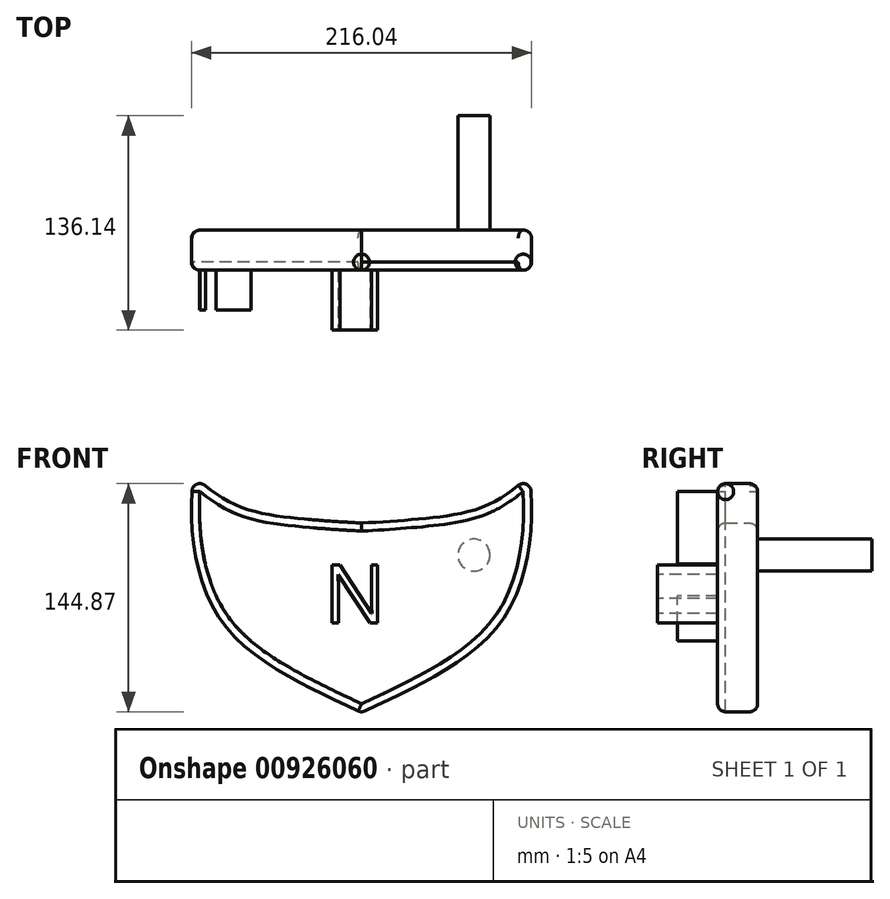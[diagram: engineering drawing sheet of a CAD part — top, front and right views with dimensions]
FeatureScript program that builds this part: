
annotation { "Feature Type Name" : "Feature", "Feature Type Description" : "" }
export const myFeature = defineFeature(function(context is Context, id is Id, definition is map)
    precondition{}
    {
        {
            var Q0;
            Q0=qCreatedBy(makeId("Front.planeOp"),FACE);
            var sketch = newSketch(context, id + "F0", { "sketchPlane" : qUnion([Q0])});
            skLineSegment(sketch, "E0", {"start": v(0, 53.5) * mm, "end": v(0, -66.83) * mm});
            skFitSpline(sketch, "E1", {"points": [v(-107.19, 83.77) * mm, v(-80.88, 65.4) * mm, v(-46.3, 57.1) * mm, v(0, 53.5) * mm], "startDerivative": vector(81.22, -67.73) * mm, "endDerivative": vector(128.95, -7.74) * mm});
            skFitSpline(sketch, "E2", {"points": [v(-107.19, 83.77) * mm, v(-107.19, 44.86) * mm, v(-85.57, -13.15) * mm, v(0, -66.83) * mm], "startDerivative": vector(-8.43, -141.7) * mm, "endDerivative": vector(241.74, -112.08) * mm});
            skFitSpline(sketch, "E3.MirrorCS", {"points": [v(107.19, 83.77) * mm, v(80.88, 65.4) * mm, v(46.3, 57.1) * mm, v(0, 53.5) * mm], "startDerivative": vector(-81.22, -67.73) * mm, "endDerivative": vector(-128.95, -7.74) * mm});
            skFitSpline(sketch, "E4.MirrorCS", {"points": [v(107.19, 83.77) * mm, v(107.19, 44.86) * mm, v(85.57, -13.15) * mm, v(0, -66.83) * mm], "startDerivative": vector(8.43, -141.7) * mm, "endDerivative": vector(-241.74, -112.08) * mm});
            skSolve(sketch);
        }
        {
            var Q0;
            Q0=makeQuery(id+"F0.imprint","IMPRINT",FACE,{"disambiguationData":[TD([[makeQuery(id+"F0.imprint","IMPRINT",EDGE,{"derivedFrom":sQuery(id+"F0.wireOp",EDGE,"E0")}),-1.0]])]});
            var Q1;
            Q1=makeQuery(id+"F0.imprint","IMPRINT",FACE,{"disambiguationData":[TD([[makeQuery(id+"F0.imprint","IMPRINT",EDGE,{"derivedFrom":sQuery(id+"F0.wireOp",EDGE,"E0")}),1.0]])]});
            extrude(context, id + "F1", {"entities" : qUnion([Q0, Q1]), "depth" : 25.4 * mm, "offsetDistance" : 25.4 * mm});
        }
        {
            var Q0;
            Q0=makeQuery(id+"F1.opExtrude","CAP_EDGE",EDGE,{"disambiguationData":[OSD([sQuery(id+"F0.wireOp",EDGE,"E2")])],"isStart":true});
            var Q1;
            Q1=makeQuery(id+"F1.opExtrude","CAP_EDGE",EDGE,{"disambiguationData":[OSD([sQuery(id+"F0.wireOp",EDGE,"E2")])],"isStart":false});
            fillet(context, id + "F2", {"entities" : qUnion([Q0, Q1]), "radius" : 5.08 * mm, "tangentPropagation" : true, "allowEdgeOverflow" : false});
        }
        {
            var Q0;
            Q0=makeQuery(id+"F1.opExtrude","CAP_EDGE",EDGE,{"disambiguationData":[OSD([sQuery(id+"F0.wireOp",EDGE,"E3.MirrorCS")])],"isStart":true});
            var Q1;
            Q1=makeQuery(id+"F1.opExtrude","CAP_FACE",FACE,{"disambiguationData":[OSD([sQuery(id+"F0.wireOp",EDGE,"E1"),sQuery(id+"F0.wireOp",EDGE,"E2"),sQuery(id+"F0.wireOp",EDGE,"E3.MirrorCS"),sQuery(id+"F0.wireOp",EDGE,"E4.MirrorCS")])],"isStart":false});
            fillet(context, id + "F3", {"entities" : qUnion([Q0, Q1]), "radius" : 5.08 * mm, "tangentPropagation" : true, "allowEdgeOverflow" : false});
        }
        {
            var Q0;
            Q0=makeQuery(id+"F3.opFillet","BLEND_EDGE",EDGE,{"blendedFrom":[makeQuery(id+"F1.opExtrude","CAP_EDGE",EDGE,{"disambiguationData":[OSD([sQuery(id+"F0.wireOp",EDGE,"E3.MirrorCS")])],"isStart":false}),makeQuery(id+"F1.opExtrude","CAP_EDGE",EDGE,{"disambiguationData":[OSD([sQuery(id+"F0.wireOp",EDGE,"E4.MirrorCS")])],"isStart":false})],"blendedInto":[]});
            var Q1;
            {var subQ0=sQuery(id+"F0.wireOp",EDGE,"E1");Q1=makeQuery(id+"F3.opFillet","BLEND_EDGE",EDGE,{"blendedFrom":[makeQuery(id+"F1.opExtrude","CAP_EDGE",EDGE,{"disambiguationData":[OSD([subQ0])],"isStart":false}),makeQuery(id+"F1.opExtrude","SWEPT_FACE",FACE,{"disambiguationData":[OSD([subQ0])]})],"blendedInto":[makeQuery(id+"F1.opExtrude","SWEPT_FACE",FACE,{"disambiguationData":[OSD([subQ0])]})]});}
            var Q2;
            {var subQ0=sQuery(id+"F0.wireOp",EDGE,"E2");Q2=makeQuery(id+"F2.opFillet","BLEND_EDGE",EDGE,{"blendedFrom":[makeQuery(id+"F1.opExtrude","CAP_EDGE",EDGE,{"disambiguationData":[OSD([subQ0])],"isStart":true}),makeQuery(id+"F1.opExtrude","SWEPT_FACE",FACE,{"disambiguationData":[OSD([subQ0])]})],"blendedInto":[makeQuery(id+"F1.opExtrude","SWEPT_FACE",FACE,{"disambiguationData":[OSD([subQ0])]})]});}
            var Q3;
            {var subQ0=sQuery(id+"F0.wireOp",EDGE,"E1");var subQ1=sQuery(id+"F0.wireOp",EDGE,"E2");Q3=makeQuery(id+"F3.opFillet","BLEND_EDGE",EDGE,{"blendedFrom":[makeQuery(id+"F1.opExtrude","SWEPT_EDGE",EDGE,{"disambiguationData":[OSD([subQ0,subQ1])]}),makeQuery(id+"F2.opFillet","BLEND_EDGE",EDGE,{"blendedFrom":[makeQuery(id+"F1.opExtrude","CAP_EDGE",EDGE,{"disambiguationData":[OSD([subQ1])],"isStart":false}),makeQuery(id+"F1.opExtrude","SWEPT_FACE",FACE,{"disambiguationData":[OSD([subQ0])]})],"blendedInto":[makeQuery(id+"F1.opExtrude","SWEPT_FACE",FACE,{"disambiguationData":[OSD([subQ0])]})]})],"blendedInto":[]});}
            fillet(context, id + "F4", {"entities" : qUnion([Q0, Q1, Q2, Q3]), "radius" : 5.08 * mm, "tangentPropagation" : true, "allowEdgeOverflow" : false});
        }
        {
            var Q0;
            Q0=makeQuery(id+"F1.opExtrude","CAP_FACE",FACE,{"disambiguationData":[OSD([sQuery(id+"F0.wireOp",EDGE,"E1"),sQuery(id+"F0.wireOp",EDGE,"E2"),sQuery(id+"F0.wireOp",EDGE,"E3.MirrorCS"),sQuery(id+"F0.wireOp",EDGE,"E4.MirrorCS")])],"isStart":true});
            var sketch = newSketch(context, id + "F5", { "sketchPlane" : qUnion([Q0])});
            skSolve(sketch);
        }
        {
            var Q0;
            Q0=qCreatedBy(makeId("Front.planeOp"),FACE);
            var sketch = newSketch(context, id + "F6", { "sketchPlane" : qUnion([Q0])});
            skText(sketch, "E5", { "text": "DEVIL\n", "fontName": "OpenSans-Bold.ttf"});
            const initialGuessF6  = {"E5": [-0.04514, -0.01103, 1, 0, 0.03178]};
            skSetInitialGuess(sketch, initialGuessF6);
            skSolve(sketch);
        }
        {
            var Q0;
            Q0=qCreatedBy(makeId("Front.planeOp"),FACE);
            var sketch = newSketch(context, id + "F7", { "sketchPlane" : qUnion([Q0])});
            skSolve(sketch);
        }
        {
            var Q0;
            Q0 = qSketchRegion(id + "F6", true);
            var Q1;
            Q1=makeQuery(id+"F1.opExtrude","CAP_FACE",FACE,{"disambiguationData":[OSD([sQuery(id+"F0.wireOp",EDGE,"E1"),sQuery(id+"F0.wireOp",EDGE,"E2"),sQuery(id+"F0.wireOp",EDGE,"E3.MirrorCS"),sQuery(id+"F0.wireOp",EDGE,"E4.MirrorCS")])],"isStart":false});
            var Q2;
            {var subQ0=sQuery(id+"F0.wireOp",EDGE,"E4.MirrorCS");var subQ1=sQuery(id+"F0.wireOp",EDGE,"E3.MirrorCS");var subQ2=sQuery(id+"F0.wireOp",EDGE,"E2");var subQ3=sQuery(id+"F0.wireOp",EDGE,"E1");var subQ4=makeQuery(id+"F1.opExtrude","CAP_FACE",FACE,{"disambiguationData":[OSD([subQ3,subQ2,subQ1,subQ0])],"isStart":true});var subQ5=subQ4;Q2=makeQuery(id+"F5.imprint","IMPRINT",FACE,{"disambiguationData":[TD([[makeQuery(id+"F5.imprint","IMPRINT",EDGE,{"derivedFrom":makeQuery(id+"F3.opFillet","BLEND_EDGE",EDGE,{"blendedFrom":[makeQuery(id+"F1.opExtrude","CAP_EDGE",EDGE,{"disambiguationData":[OSD([subQ1])],"isStart":true}),subQ5],"blendedInto":[subQ5]})}),1.0]])]});}
            var Q3;
            Q3=makeQuery(id+"F6.imprint","IMPRINT",FACE,{"disambiguationData":[TD([[makeQuery(id+"F6.imprint","IMPRINT",EDGE,{"derivedFrom":sQuery(id+"F6.wireOp",EDGE,"E5.sketch_text.stroke-24")}),-1.0]])]});
            var Q4;
            Q4=makeQuery(id+"F6.imprint","IMPRINT",FACE,{"disambiguationData":[TD([[makeQuery(id+"F6.imprint","IMPRINT",EDGE,{"derivedFrom":sQuery(id+"F6.wireOp",EDGE,"E5.sketch_text.stroke-34")}),-1.0]])]});
            var Q5;
            Q5=makeQuery(id+"F1.opExtrude","CAP_FACE",FACE,{"disambiguationData":[OSD([sQuery(id+"F0.wireOp",EDGE,"E1"),sQuery(id+"F0.wireOp",EDGE,"E2"),sQuery(id+"F0.wireOp",EDGE,"E3.MirrorCS"),sQuery(id+"F0.wireOp",EDGE,"E4.MirrorCS")])],"isStart":true});
            var Q6;
            Q6=makeQuery(id+"F6.imprint","IMPRINT",FACE,{"disambiguationData":[TD([[makeQuery(id+"F6.imprint","IMPRINT",EDGE,{"derivedFrom":sQuery(id+"F6.wireOp",EDGE,"E5.sketch_text.stroke-0")}),-1.0]])]});
            var Q7;
            Q7=makeQuery(id+"F6.imprint","IMPRINT",FACE,{"disambiguationData":[TD([[makeQuery(id+"F6.imprint","IMPRINT",EDGE,{"derivedFrom":sQuery(id+"F6.wireOp",EDGE,"E5.sketch_text.stroke-7")}),1.0]])]});
            var Q8;
            Q8=makeQuery(id+"F6.imprint","IMPRINT",FACE,{"disambiguationData":[TD([[makeQuery(id+"F6.imprint","IMPRINT",EDGE,{"derivedFrom":sQuery(id+"F6.wireOp",EDGE,"E5.sketch_text.stroke-12")}),-1.0]])]});
            var Q9;
            Q9=makeQuery(id+"F6.imprint","IMPRINT",FACE,{"disambiguationData":[TD([[makeQuery(id+"F6.imprint","IMPRINT",EDGE,{"derivedFrom":sQuery(id+"F6.wireOp",EDGE,"E5.sketch_text.stroke-38")}),-1.0]])]});
            extrude(context, id + "F8", {"entities" : qUnion([Q0, Q1, Q2, Q3, Q4, Q5, Q6, Q7, Q8, Q9]), "operationType" : NewBodyOperationType.ADD, "depth" : 25.4 * mm, "offsetDistance" : 25.4 * mm});
        }
        {
            var Q0;
            {var subQ0=sQuery(id+"F0.wireOp",EDGE,"E4.MirrorCS");var subQ1=sQuery(id+"F0.wireOp",EDGE,"E3.MirrorCS");var subQ2=sQuery(id+"F0.wireOp",EDGE,"E2");var subQ3=sQuery(id+"F0.wireOp",EDGE,"E1");Q0=makeQuery(id+"F8.opExtrude","CAP_FACE",FACE,{"disambiguationData":[OSD([subQ3,subQ2,subQ1,subQ0]),TDD([makeQuery(id+"F1.opExtrude","CAP_FACE",FACE,{"disambiguationData":[OSD([subQ3,subQ2,subQ1,subQ0])],"isStart":false})])],"isStart":false});}
            var sketch = newSketch(context, id + "F9", { "sketchPlane" : qUnion([Q0])});
            skText(sketch, "E6", { "text": "N\n", "fontName": "OpenSans-Regular.ttf"});
            const initialGuessF9  = {"E6": [-0.02372, -0.01007, 1, 0, 0.0373]};
            skSetInitialGuess(sketch, initialGuessF9);
            skSolve(sketch);
        }
        {
            var Q0;
            Q0 = qSketchRegion(id + "F9", true);
            extrude(context, id + "F10", {"entities" : qUnion([Q0]), "operationType" : NewBodyOperationType.ADD, "depth" : 12.7 * mm, "offsetDistance" : 25.4 * mm});
        }
        {
            var Q0;
            Q0=qCreatedBy(makeId("Front.planeOp"),FACE);
            var sketch = newSketch(context, id + "F11", { "sketchPlane" : qUnion([Q0])});
            skCircle(sketch, "E7", {"center": v(80.37, 37.2) * mm, "radius": 12.45 * mm});
            skSolve(sketch);
        }
        {
            var Q0;
            Q0=makeQuery(id+"F11.imprint","IMPRINT",FACE,{"disambiguationData":[TD([[makeQuery(id+"F11.imprint","IMPRINT",EDGE,{"derivedFrom":sQuery(id+"F11.wireOp",EDGE,"E7")}),1.0]])]});
            var Q1;
            Q1=makeQuery(id+"F1.opExtrude","CAP_FACE",FACE,{"disambiguationData":[OSD([sQuery(id+"F0.wireOp",EDGE,"E1"),sQuery(id+"F0.wireOp",EDGE,"E2"),sQuery(id+"F0.wireOp",EDGE,"E3.MirrorCS"),sQuery(id+"F0.wireOp",EDGE,"E4.MirrorCS")])],"isStart":true});
            var Q2;
            {var subQ0=sQuery(id+"F0.wireOp",EDGE,"E4.MirrorCS");var subQ1=sQuery(id+"F0.wireOp",EDGE,"E3.MirrorCS");var subQ2=sQuery(id+"F0.wireOp",EDGE,"E2");var subQ3=sQuery(id+"F0.wireOp",EDGE,"E1");Q2=makeQuery(id+"F8.opExtrude","CAP_FACE",FACE,{"disambiguationData":[OSD([subQ3,subQ2,subQ1,subQ0]),TDD([makeQuery(id+"F1.opExtrude","CAP_FACE",FACE,{"disambiguationData":[OSD([subQ3,subQ2,subQ1,subQ0])],"isStart":false})])],"isStart":false});}
            extrude(context, id + "F12", {"entities" : qUnion([Q0, Q1, Q2]), "operationType" : NewBodyOperationType.REMOVE, "oppositeDirection" : true, "depth" : 25.4 * mm, "offsetDistance" : 25.4 * mm});
        }
        {
            var Q0;
            Q0=qCreatedBy(makeId("Front.planeOp"),FACE);
            var sketch = newSketch(context, id + "F13", { "sketchPlane" : qUnion([Q0])});
            skCircle(sketch, "E8", {"center": v(71.4, 33.17) * mm, "radius": 10.17 * mm});
            skSolve(sketch);
        }
        {
            var Q0;
            Q0 = qSketchRegion(id + "F7", true);
            var Q1;
            Q1 = qSketchRegion(id + "F13", true);
            extrude(context, id + "F14", {"entities" : qUnion([Q0, Q1]), "operationType" : NewBodyOperationType.ADD, "oppositeDirection" : true, "depth" : 72.64 * mm, "offsetDistance" : 25.4 * mm});
        }
    });
